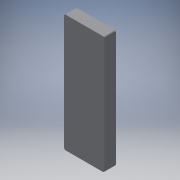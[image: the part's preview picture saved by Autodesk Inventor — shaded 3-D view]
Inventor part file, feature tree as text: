
AUTODESK INVENTOR PART (.ipt)
format: ipt  version: 2018 (Build 220112000, 112)  size: 126,976 bytes
history: native  units: in
note: dims shown in document units (in); Inventor stores cm internally (conversion verified against a paired STEP export)
features: reference x6, other x5, sketch x2, extrude x2, plane x1, fillet x1
ambient origin geometry x8: Origin, YZ Plane, XZ Plane, XY Plane, X Axis, Y Axis, Z Axis, Center Point
bodies: Solid1 (feature_tree)
feature tree (17):
  sketch  "Sketch1"  dims[d0=0.1in d1=0.0in d8=0.0394in d11=0.1181in]
  plane  "Work Plane1"
  extrude  "Extrusion1"  Depth=0.0394in
  fillet  "Fillet1"  Radius=0.1181in
  extrude  "Extrusion3"  Depth=0.1969in
  reference  "Reference1"
  reference  "Reference2"
  reference  "Reference3"
  reference  "Reference4"
  reference  "Reference5"
  reference  "Reference6"
  sketch  "Sketch3"  dims[d12=0.1575in d13=0.0984in d14=0.1575in d16=0.1969in d17=0.0in]
  other  "<userpath>\OneDrive\Documents\Inventor\TSA\2018\Animatronics\Tortoise\AssemblyTURTLE.iam"
  other  "AssemblyTURTLE.iam"
  other  "AssemblyNEWarm:1"
  other  "newShoulder:1"
  other  "Rack:5"
